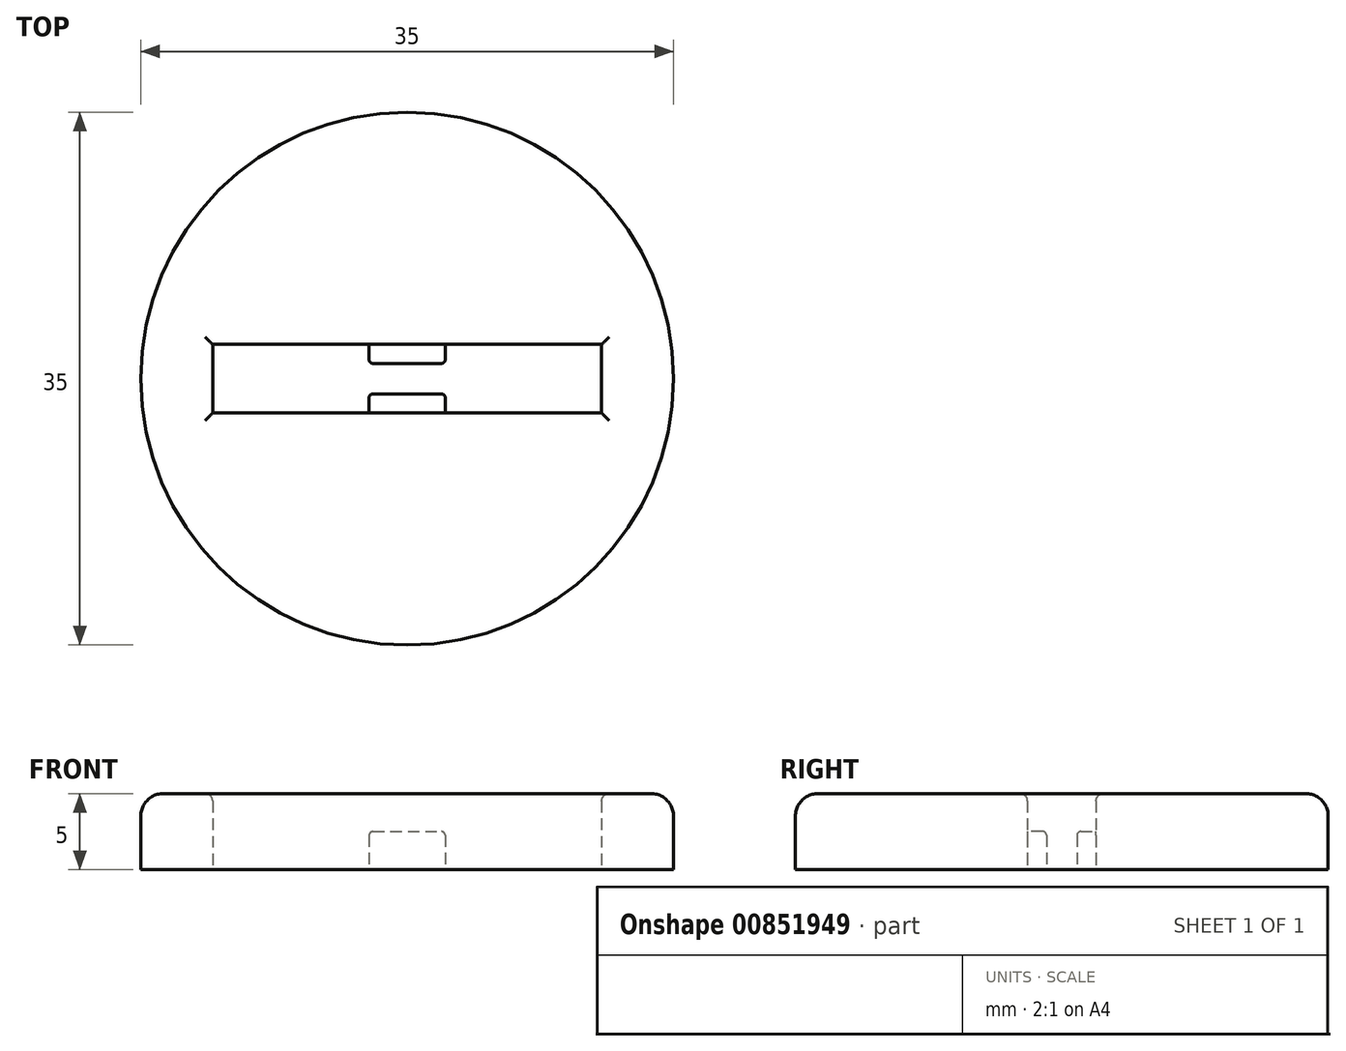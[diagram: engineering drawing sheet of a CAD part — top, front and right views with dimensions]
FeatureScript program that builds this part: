
annotation { "Feature Type Name" : "Feature", "Feature Type Description" : "" }
export const myFeature = defineFeature(function(context is Context, id is Id, definition is map)
    precondition{}
    {
        {
            var Q0;
            Q0=qCreatedBy(makeId("Top.planeOp"),FACE);
            var sketch = newSketch(context, id + "F0", { "sketchPlane" : qUnion([Q0])});
            skPoint(sketch, "E0.middle", {"position": v(0, 0) * mm});
            skLineSegment(sketch, "E1.bottom", {"start": v(-12.78, 2.25) * mm, "end": v(12.78, 2.25) * mm});
            skLineSegment(sketch, "E1.top", {"start": v(-12.78, -2.25) * mm, "end": v(12.78, -2.25) * mm});
            skLineSegment(sketch, "E1.left", {"start": v(-12.78, 2.25) * mm, "end": v(-12.78, -2.25) * mm});
            skLineSegment(sketch, "E1.right", {"start": v(12.78, 2.25) * mm, "end": v(12.78, -2.25) * mm});
            skLineSegment(sketch, "E2", {"start": v(-2.5, -1) * mm, "end": v(-2.5, -2.25) * mm});
            skLineSegment(sketch, "E3", {"start": v(2.5, -1) * mm, "end": v(2.5, -2.25) * mm});
            skLineSegment(sketch, "E4", {"start": v(2.5, 1) * mm, "end": v(2.5, 2.25) * mm});
            skLineSegment(sketch, "E5", {"start": v(-2.5, 1) * mm, "end": v(-2.5, 2.25) * mm});
            skLineSegment(sketch, "E6", {"start": v(2.5, -1) * mm, "end": v(-2.5, -1) * mm});
            skLineSegment(sketch, "E7", {"start": v(-2.5, 1) * mm, "end": v(2.5, 1) * mm});
            skCircle(sketch, "E8", {"center": v(0, 0) * mm, "radius": 17.5 * mm});
            skSolve(sketch);
        }
        {
            var Q0;
            Q0 = qSketchRegion(id + "F0", true);
            extrude(context, id + "F1", {"entities" : qUnion([Q0]), "depth" : 5 * mm, "offsetDistance" : 25 * mm});
        }
        {
            var Q0;
            {var subQ0=sQuery(id+"F0.wireOp",EDGE,"E4");Q0=makeQuery(id+"F0.imprint","IMPRINT",FACE,{"disambiguationData":[TD([[makeQuery(id+"F0.imprint","IMPRINT",EDGE,{"derivedFrom":subQ0}),1.0]])]});}
            var Q1;
            {var subQ0=sQuery(id+"F0.wireOp",EDGE,"E2");Q1=makeQuery(id+"F0.imprint","IMPRINT",FACE,{"disambiguationData":[TD([[makeQuery(id+"F0.imprint","IMPRINT",EDGE,{"derivedFrom":subQ0}),1.0]])]});}
            extrude(context, id + "F2", {"entities" : qUnion([Q0, Q1]), "operationType" : NewBodyOperationType.ADD, "depth" : 2.5 * mm, "offsetDistance" : 25 * mm});
        }
        {
            var Q0;
            Q0=makeQuery(id+"F2.opExtrude","SWEPT_EDGE",EDGE,{"disambiguationData":[OSD([sQuery(id+"F0.wireOp",EDGE,"E2"),sQuery(id+"F0.wireOp",EDGE,"E6")])]});
            var Q1;
            Q1=makeQuery(id+"F2.opExtrude","CAP_EDGE",EDGE,{"disambiguationData":[OSD([sQuery(id+"F0.wireOp",EDGE,"E2")])],"isStart":false});
            var Q2;
            Q2=makeQuery(id+"F2.opExtrude","CAP_EDGE",EDGE,{"disambiguationData":[OSD([sQuery(id+"F0.wireOp",EDGE,"E6")])],"isStart":false});
            var Q3;
            Q3=makeQuery(id+"F2.opExtrude","CAP_EDGE",EDGE,{"disambiguationData":[OSD([sQuery(id+"F0.wireOp",EDGE,"E3")])],"isStart":false});
            var Q4;
            Q4=makeQuery(id+"F2.opExtrude","CAP_EDGE",EDGE,{"disambiguationData":[OSD([sQuery(id+"F0.wireOp",EDGE,"E7")])],"isStart":false});
            var Q5;
            Q5=makeQuery(id+"F2.opExtrude","CAP_EDGE",EDGE,{"disambiguationData":[OSD([sQuery(id+"F0.wireOp",EDGE,"E4")])],"isStart":false});
            var Q6;
            Q6=makeQuery(id+"F2.opExtrude","CAP_EDGE",EDGE,{"disambiguationData":[OSD([sQuery(id+"F0.wireOp",EDGE,"E5")])],"isStart":false});
            var Q7;
            Q7=makeQuery(id+"F2.opExtrude","SWEPT_EDGE",EDGE,{"disambiguationData":[OSD([sQuery(id+"F0.wireOp",EDGE,"E5"),sQuery(id+"F0.wireOp",EDGE,"E7")])]});
            var Q8;
            Q8=makeQuery(id+"F2.opExtrude","SWEPT_EDGE",EDGE,{"disambiguationData":[OSD([sQuery(id+"F0.wireOp",EDGE,"E3"),sQuery(id+"F0.wireOp",EDGE,"E6")])]});
            var Q9;
            Q9=makeQuery(id+"F2.opExtrude","SWEPT_EDGE",EDGE,{"disambiguationData":[OSD([sQuery(id+"F0.wireOp",EDGE,"E4"),sQuery(id+"F0.wireOp",EDGE,"E7")])]});
            fillet(context, id + "F3", {"entities" : qUnion([Q0, Q1, Q2, Q3, Q4, Q5, Q6, Q7, Q8, Q9]), "radius" : .25 * mm, "tangentPropagation" : true, "allowEdgeOverflow" : false});
        }
        {
            var Q0;
            Q0=makeQuery(id+"F1.opExtrude","CAP_EDGE",EDGE,{"disambiguationData":[OSD([sQuery(id+"F0.wireOp",EDGE,"E1.bottom")])],"isStart":false});
            var Q1;
            Q1=makeQuery(id+"F1.opExtrude","CAP_EDGE",EDGE,{"disambiguationData":[OSD([sQuery(id+"F0.wireOp",EDGE,"E1.right")])],"isStart":false});
            var Q2;
            Q2=makeQuery(id+"F1.opExtrude","CAP_EDGE",EDGE,{"disambiguationData":[OSD([sQuery(id+"F0.wireOp",EDGE,"E1.top")])],"isStart":false});
            var Q3;
            Q3=makeQuery(id+"F1.opExtrude","CAP_EDGE",EDGE,{"disambiguationData":[OSD([sQuery(id+"F0.wireOp",EDGE,"E1.left")])],"isStart":false});
            fillet(context, id + "F4", {"entities" : qUnion([Q0, Q1, Q2, Q3]), "radius" : .5 * mm, "tangentPropagation" : true, "allowEdgeOverflow" : false});
        }
        {
            var Q0;
            Q0=makeQuery(id+"F1.opExtrude","CAP_EDGE",EDGE,{"disambiguationData":[OSD([sQuery(id+"F0.wireOp",EDGE,"E8")])],"isStart":false});
            fillet(context, id + "F5", {"entities" : qUnion([Q0]), "radius" : 1.5 * mm, "tangentPropagation" : true, "allowEdgeOverflow" : false});
        }
    });
